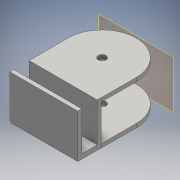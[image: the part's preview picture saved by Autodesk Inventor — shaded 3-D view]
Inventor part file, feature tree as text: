
AUTODESK INVENTOR PART (.ipt)
format: ipt  version: 2016 (Build 200138000, 138)  size: 125,952 bytes
history: native  units: mm
features: sketch x4, extrude x3, plane x1
ambient origin geometry x8: Origin, YZ Plane, XZ Plane, XY Plane, X Axis, Y Axis, Z Axis, Center Point
bodies: Solid1 (feature_tree)
feature tree (8):
  extrude  "Extrusion1"  Depth=12.0mm
  extrude  "Extrusion2"  Depth=18.0mm
  sketch  "Sketch3"  dims[d7=22.5mm d8=0.0mm d9=20.0mm d10=0.0mm]
  plane  "Work Plane1"
  extrude  "Extrusion3"  Depth=20.0mm TaperAngle=0.0deg
  sketch  "Sketch1"  dims[d0=35.0mm d1=12.0mm]
  sketch  "Sketch2"  dims[d4=18.0mm d6=4.0mm]
  sketch  "Sketch4"  dims[d11=18.5mm d12=2.0mm d13=35.5mm d14=0.0mm]
